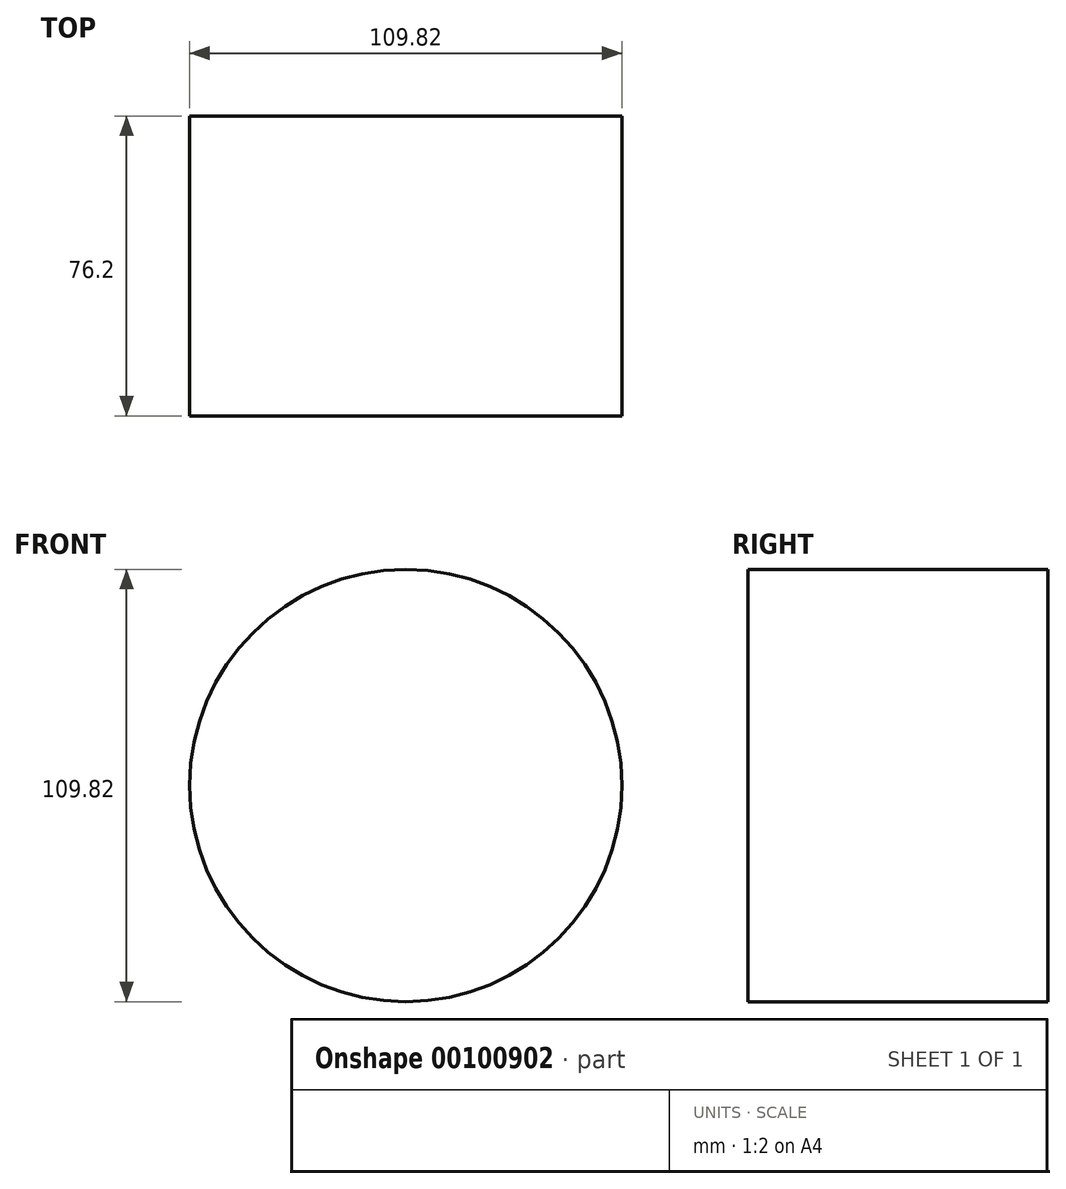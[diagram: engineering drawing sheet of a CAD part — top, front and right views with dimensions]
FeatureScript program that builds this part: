
annotation { "Feature Type Name" : "Feature", "Feature Type Description" : "" }
export const myFeature = defineFeature(function(context is Context, id is Id, definition is map)
    precondition{}
    {
        {
            var Q0;
            Q0=qCreatedBy(makeId("Front.planeOp"),FACE);
            var sketch = newSketch(context, id + "F0", { "sketchPlane" : qUnion([Q0])});
            skCircle(sketch, "E0", {"center": v(0, 0) * mm, "radius": 54.9 * mm});
            skSolve(sketch);
        }
        {
            var Q0;
            Q0=makeQuery(id+"F0.imprint","IMPRINT",FACE,{"disambiguationData":[TD([[makeQuery(id+"F0.imprint","IMPRINT",EDGE,{"derivedFrom":sQuery(id+"F0.wireOp",EDGE,"E0")}),1.0]])]});
            extrude(context, id + "F1", {"entities" : qUnion([Q0]), "depth" : 76.2 * mm});
        }
        {
            var Q0;
            Q0=makeQuery(id+"F1.opExtrude","CAP_FACE",FACE,{"disambiguationData":[OSD([sQuery(id+"F0.wireOp",EDGE,"E0")])],"isStart":false});
            var sketch = newSketch(context, id + "F2", { "sketchPlane" : qUnion([Q0])});
            skCircle(sketch, "E1", {"center": v(0, 0) * mm, "radius": 47.18 * mm});
            skCircle(sketch, "E2", {"center": v(0, 0) * mm, "radius": 41.66 * mm});
            skSolve(sketch);
        }
    });
